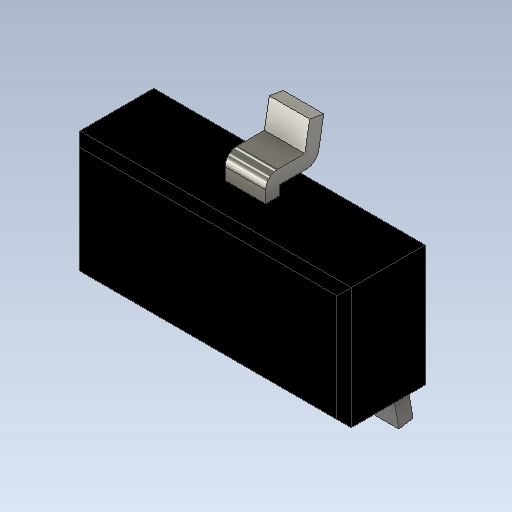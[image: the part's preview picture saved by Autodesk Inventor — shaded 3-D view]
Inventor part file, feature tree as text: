
AUTODESK INVENTOR PART (.ipt)
format: ipt  version: 2020 (Build 240168000, 168)  size: 195,072 bytes
history: native  units: in
note: dims shown in document units (in); Inventor stores cm internally (conversion verified against a paired STEP export)
features: sketch x5, sweep x2, extrude x1, chamfer x1
ambient origin geometry x8: Origin, YZ Plane, XZ Plane, XY Plane, X Axis, Y Axis, Z Axis, Center Point
bodies: Solid1 (feature_tree)
feature tree (9):
  extrude  "Extrusion1"  Depth=0.051in
  chamfer  "Chamfer1"  Distance=0.037in
  sweep  "Sweep1"
  sweep  "Sweep2"
  sketch  "Sketch1"  dims[d0=0.114in d1=0.051in d2=0.037in d3=0.0in]
  sketch  "Sketch2"  dims[d4=0.003in d5=0.125in d6=45.0deg d7=0.017in]
  sketch  "Sketch3"  dims[d8=0.006in d9=0.021in]
  sketch  "Sketch4"  dims[d10=0.007in]
  sketch  "Sketch5"  dims[d11=0.0687in d12=0.002in d13=0.0in d14=0.0in d15=0.017in d16=0.006in d17=0.075in d18=0.0375in d20=0.007in d21=0.0687in d22=0.002in d23=0.0in d24=0.0in]
